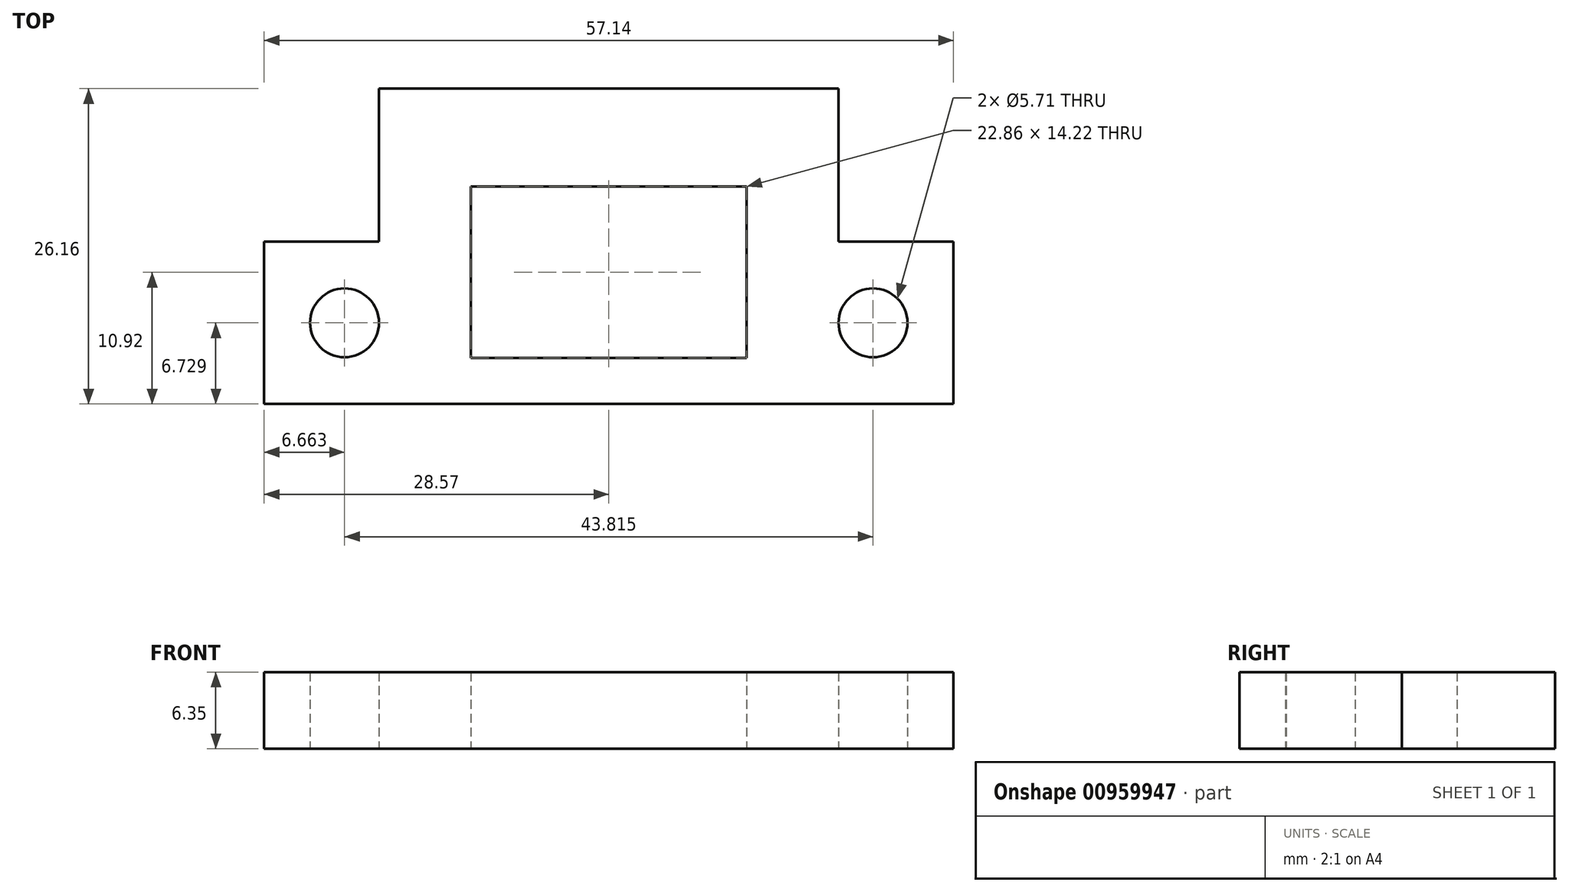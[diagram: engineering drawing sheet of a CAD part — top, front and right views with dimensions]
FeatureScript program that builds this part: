
annotation { "Feature Type Name" : "Feature", "Feature Type Description" : "" }
export const myFeature = defineFeature(function(context is Context, id is Id, definition is map)
    precondition{}
    {
        {
            var Q0;
            Q0=qCreatedBy(makeId("Top.planeOp"),FACE);
            var sketch = newSketch(context, id + "F0", { "sketchPlane" : qUnion([Q0])});
            skPoint(sketch, "E0.middle", {"position": v(0, 0) * mm});
            skLineSegment(sketch, "E1", {"start": v(-19.05, 0) * mm, "end": v(-19.05, -12.7) * mm});
            skLineSegment(sketch, "E2", {"start": v(-19.05, -12.7) * mm, "end": v(-28.58, -12.7) * mm});
            skLineSegment(sketch, "E3", {"start": v(19.05, 0) * mm, "end": v(19.05, -12.7) * mm});
            skLineSegment(sketch, "E4", {"start": v(19.05, -12.7) * mm, "end": v(28.58, -12.7) * mm});
            skLineSegment(sketch, "E5.bottom", {"start": v(11.43, -22.35) * mm, "end": v(-11.43, -22.35) * mm});
            skLineSegment(sketch, "E5.left", {"start": v(11.43, -22.35) * mm, "end": v(11.43, -8.13) * mm});
            skLineSegment(sketch, "E5.right", {"start": v(-11.43, -22.35) * mm, "end": v(-11.43, -8.13) * mm});
            skPoint(sketch, "E5.middle", {"position": v(0, -15.24) * mm});
            skCircle(sketch, "E6", {"center": v(21.9, -19.43) * mm, "radius": 2.86 * mm});
            skCircle(sketch, "E7", {"center": v(-21.9, -19.43) * mm, "radius": 2.86 * mm});
            skLineSegment(sketch, "E8", {"start": v(-11.43, -8.13) * mm, "end": v(11.43, -8.13) * mm});
            skLineSegment(sketch, "E9", {"start": v(-28.58, -12.7) * mm, "end": v(-28.58, -26.16) * mm});
            skLineSegment(sketch, "E10", {"start": v(-19.05, 0) * mm, "end": v(19.05, 0) * mm});
            skLineSegment(sketch, "E11", {"start": v(28.58, -12.7) * mm, "end": v(28.58, -26.16) * mm});
            skLineSegment(sketch, "E12", {"start": v(0, 0) * mm, "end": v(0, -26.72) * mm, "construction": true});
            skLineSegment(sketch, "E13", {"start": v(-28.58, -19.43) * mm, "end": v(28.58, -19.43) * mm, "construction": true});
            skLineSegment(sketch, "E14", {"start": v(-28.58, -26.16) * mm, "end": v(28.58, -26.16) * mm});
            skSolve(sketch);
        }
        {
            var Q0;
            Q0 = qSketchRegion(id + "F0", true);
            extrude(context, id + "F1", {"entities" : qUnion([Q0]), "depth" : 6.35 * mm, "offsetDistance" : 25.4 * mm});
        }
    });
